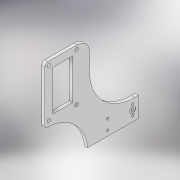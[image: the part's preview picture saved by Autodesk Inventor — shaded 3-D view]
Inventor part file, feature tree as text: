
AUTODESK INVENTOR PART (.ipt)
format: ipt  version: 2019 (Build 230136000, 136)  size: 181,760 bytes
history: native  units: mm
features: sketch x5, hole x4, extrude x1, other x1
ambient origin geometry x8: Origin, YZ Plane, XZ Plane, XY Plane, X Axis, Y Axis, Z Axis, Center Point
bodies: Solid1 (feature_tree)
feature tree (11):
  hole  "Hole1"  [1 undecoded]
  hole  "Hole2"  [1 undecoded]
  hole  "Hole3"  [1 undecoded]
  extrude  "Extrusion1"  [1 undecoded]
  hole  "Hole4"  [1 undecoded]
  sketch  "Sketch1"  dims[d0=6.756mm d1=6.0mm d2=12.878mm d3=2.0mm d4=14.3mm d5=78.0mm d6=20.594885mm]
  sketch  "Sketch2"  dims[d7=4.496mm d8=6.0mm d9=8.433mm d10=2.0mm d11=14.3mm d12=78.0mm d13=20.594885mm]
  sketch  "Sketch3"  dims[d14=4.496mm d15=6.0mm d16=8.433mm d17=2.0mm d18=14.3mm d19=78.0mm d20=20.594885mm d21=5.0mm]
  sketch  "Sketch4"  dims[d22=6.0mm d23=0.0mm]
  sketch  "Sketch5"  dims[d24=5.105mm d25=6.0mm d26=9.779mm d27=2.0mm d28=14.3mm d29=78.0mm d30=20.594885mm]
  other  "plate (2)"
note: 5 required parameter values undecoded (feature->parameter linkage not recoverable at this tier; creation-order binding heuristic only, values carry confidence <= 0.55)
